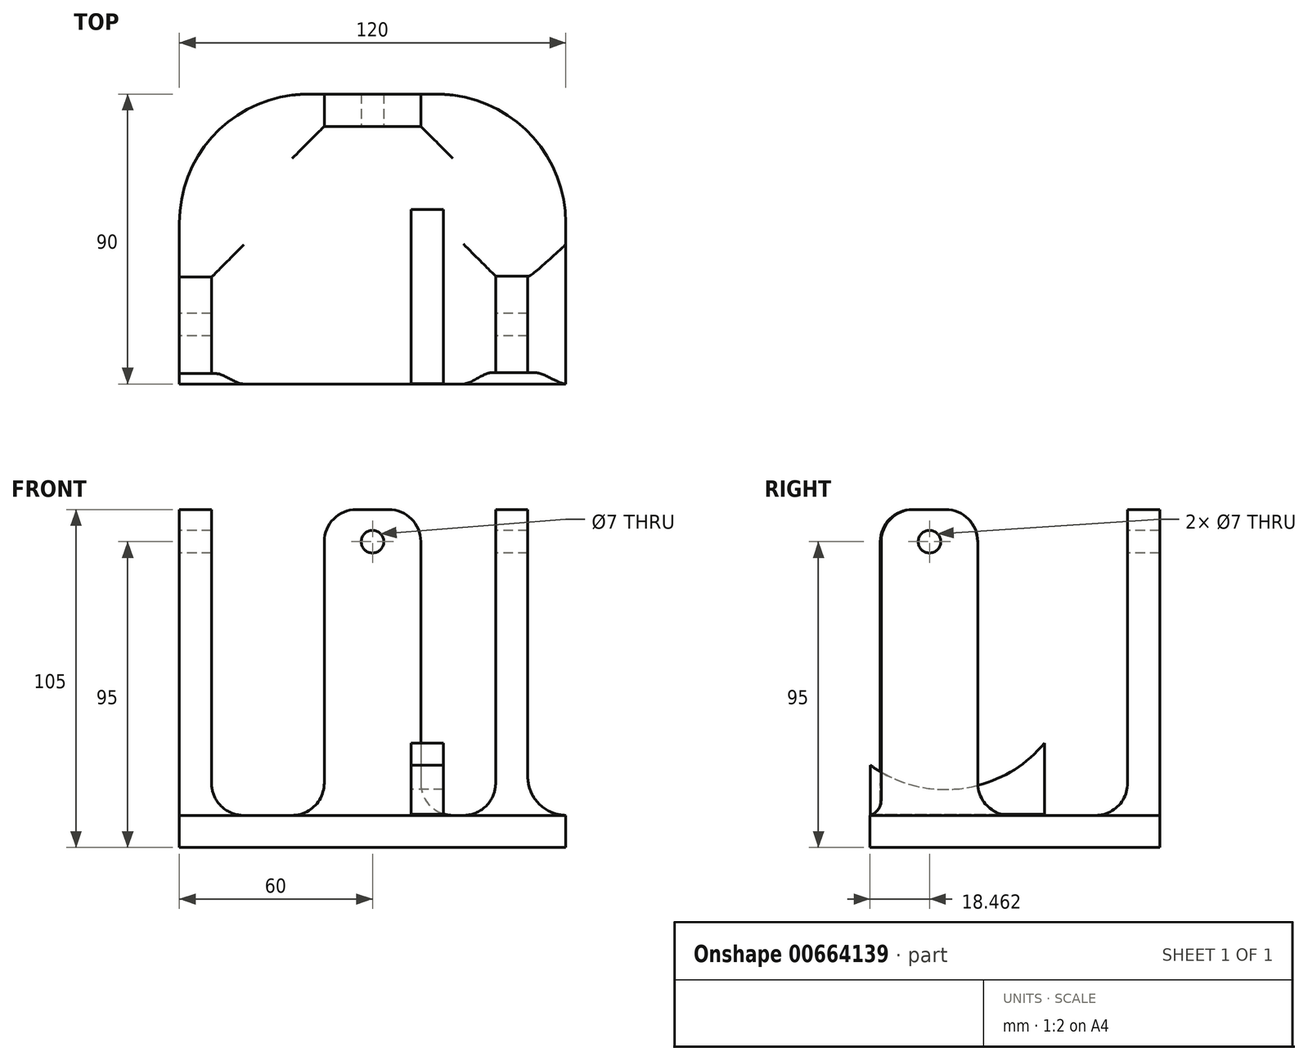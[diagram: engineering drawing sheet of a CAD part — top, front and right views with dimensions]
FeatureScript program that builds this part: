
annotation { "Feature Type Name" : "Feature", "Feature Type Description" : "" }
export const myFeature = defineFeature(function(context is Context, id is Id, definition is map)
    precondition{}
    {
        {
            var Q0;
            Q0=qCreatedBy(makeId("Top.planeOp"),FACE);
            var sketch = newSketch(context, id + "F0", { "sketchPlane" : qUnion([Q0])});
            skLineSegment(sketch, "E0.bottom", {"start": v(-20, 45) * mm, "end": v(20, 45) * mm});
            skLineSegment(sketch, "E0.top", {"start": v(-60, -45) * mm, "end": v(60, -45) * mm});
            skLineSegment(sketch, "E0.left", {"start": v(-60, 5) * mm, "end": v(-60, -45) * mm});
            skLineSegment(sketch, "E0.right", {"start": v(60, 5) * mm, "end": v(60, -45) * mm});
            skPoint(sketch, "E0.middle", {"position": v(0, 0) * mm});
            skPoint(sketch, "E1.visualSharp", {"position": v(-60, 45) * mm});
            skArc(sketch, "E1.filletArc", {"start": v(-20, 45) * mm, "mid": v(-48.28, 33.28) * mm, "end": v(-60, 5) * mm});
            skPoint(sketch, "E2.visualSharp", {"position": v(60, 45) * mm});
            skArc(sketch, "E2.filletArc", {"start": v(60, 5) * mm, "mid": v(48.28, 33.28) * mm, "end": v(20, 45) * mm});
            skSolve(sketch);
        }
        {
            var Q0;
            Q0=makeQuery(id+"F0.imprint","IMPRINT",FACE,{"disambiguationData":[TD([[makeQuery(id+"F0.imprint","IMPRINT",EDGE,{"derivedFrom":sQuery(id+"F0.wireOp",EDGE,"E0.bottom")}),-1.0]])]});
            extrude(context, id + "F1", {"entities" : qUnion([Q0]), "depth" : 10 * mm, "offsetDistance" : 25 * mm});
        }
        {
            var Q0;
            Q0=makeQuery(id+"F1.opExtrude","CAP_FACE",FACE,{"disambiguationData":[OSD([sQuery(id+"F0.wireOp",EDGE,"E0.bottom"),sQuery(id+"F0.wireOp",EDGE,"E0.top"),sQuery(id+"F0.wireOp",EDGE,"E0.left"),sQuery(id+"F0.wireOp",EDGE,"E0.right"),sQuery(id+"F0.wireOp",EDGE,"E1.filletArc"),sQuery(id+"F0.wireOp",EDGE,"E2.filletArc")])],"isStart":false});
            var sketch = newSketch(context, id + "F2", { "sketchPlane" : qUnion([Q0])});
            skSolve(sketch);
        }
        {
            var Q0;
            Q0=qCreatedBy(makeId("Top.planeOp"),FACE);
            var sketch = newSketch(context, id + "F3", { "sketchPlane" : qUnion([Q0])});
            skLineSegment(sketch, "E3.bottom", {"start": v(-60, -41.81) * mm, "end": v(-50, -41.81) * mm});
            skLineSegment(sketch, "E3.top", {"start": v(-60, -11.81) * mm, "end": v(-50, -11.81) * mm});
            skLineSegment(sketch, "E3.left", {"start": v(-60, -41.81) * mm, "end": v(-60, -11.81) * mm});
            skLineSegment(sketch, "E3.right", {"start": v(-50, -41.81) * mm, "end": v(-50, -11.81) * mm});
            skLineSegment(sketch, "E4.bottom", {"start": v(38.23, -41.54) * mm, "end": v(48.23, -41.54) * mm});
            skLineSegment(sketch, "E4.top", {"start": v(38.23, -11.54) * mm, "end": v(48.23, -11.54) * mm});
            skLineSegment(sketch, "E4.left", {"start": v(38.23, -41.54) * mm, "end": v(38.23, -11.54) * mm});
            skLineSegment(sketch, "E4.right", {"start": v(48.23, -41.54) * mm, "end": v(48.23, -11.54) * mm});
            skLineSegment(sketch, "E5.bottom", {"start": v(-15, 45) * mm, "end": v(15, 45) * mm});
            skLineSegment(sketch, "E5.top", {"start": v(-15, 35) * mm, "end": v(15, 35) * mm});
            skLineSegment(sketch, "E5.left", {"start": v(-15, 45) * mm, "end": v(-15, 35) * mm});
            skLineSegment(sketch, "E5.right", {"start": v(15, 45) * mm, "end": v(15, 35) * mm});
            skSolve(sketch);
        }
        {
            var Q0;
            Q0=qSketchRegion(id+"F3",true);
            extrude(context, id + "F4", {"entities" : qUnion([Q0]), "operationType" : NewBodyOperationType.ADD, "depth" : 25 * mm, "offsetDistance" : 25 * mm});
        }
        {
            var Q0;
            Q0=qSketchRegion(id+"F3",true);
            var Q1;
            Q1=makeQuery(id+"F4.opExtrude","CAP_FACE",FACE,{"disambiguationData":[OSD([sQuery(id+"F3.wireOp",EDGE,"E3.bottom"),sQuery(id+"F3.wireOp",EDGE,"E3.top"),sQuery(id+"F3.wireOp",EDGE,"E3.left"),sQuery(id+"F3.wireOp",EDGE,"E3.right")])],"isStart":false});
            var Q2;
            Q2=makeQuery(id+"F4.opExtrude","CAP_FACE",FACE,{"disambiguationData":[OSD([sQuery(id+"F3.wireOp",EDGE,"E5.bottom"),sQuery(id+"F3.wireOp",EDGE,"E5.top"),sQuery(id+"F3.wireOp",EDGE,"E5.left"),sQuery(id+"F3.wireOp",EDGE,"E5.right")])],"isStart":false});
            var Q3;
            Q3=makeQuery(id+"F4.opExtrude","CAP_FACE",FACE,{"disambiguationData":[OSD([sQuery(id+"F3.wireOp",EDGE,"E4.bottom"),sQuery(id+"F3.wireOp",EDGE,"E4.top"),sQuery(id+"F3.wireOp",EDGE,"E4.left"),sQuery(id+"F3.wireOp",EDGE,"E4.right")])],"isStart":false});
            extrude(context, id + "F5", {"entities" : qUnion([Q0, Q1, Q2, Q3]), "operationType" : NewBodyOperationType.ADD, "depth" : 80 * mm, "offsetDistance" : 25 * mm});
        }
        {
            var Q0;
            {var subQ0=sQuery(id+"F3.wireOp",EDGE,"E4.bottom");Q0=makeQuery(id+"F5.opExtrude","CAP_EDGE",EDGE,{"disambiguationData":[OSD([subQ0]),TDD([makeQuery(id+"F4.opExtrude","CAP_EDGE",EDGE,{"disambiguationData":[OSD([subQ0])],"isStart":false})])],"isStart":false});}
            var Q1;
            {var subQ0=sQuery(id+"F3.wireOp",EDGE,"E4.top");Q1=makeQuery(id+"F5.opExtrude","CAP_EDGE",EDGE,{"disambiguationData":[OSD([subQ0]),TDD([makeQuery(id+"F4.opExtrude","CAP_EDGE",EDGE,{"disambiguationData":[OSD([subQ0])],"isStart":false})])],"isStart":false});}
            fillet(context, id + "F6", {"entities" : qUnion([Q0, Q1]), "radius" : 10 * mm, "tangentPropagation" : true, "allowEdgeOverflow" : false});
        }
        {
            var Q0;
            {var subQ0=sQuery(id+"F3.wireOp",EDGE,"E5.right");Q0=makeQuery(id+"F5.opExtrude","CAP_EDGE",EDGE,{"disambiguationData":[OSD([subQ0]),TDD([makeQuery(id+"F4.opExtrude","CAP_EDGE",EDGE,{"disambiguationData":[OSD([subQ0])],"isStart":false})])],"isStart":false});}
            fillet(context, id + "F7", {"entities" : qUnion([Q0]), "radius" : 10 * mm, "tangentPropagation" : true, "allowEdgeOverflow" : false});
        }
        {
            var Q0;
            {var subQ0=sQuery(id+"F3.wireOp",EDGE,"E5.left");Q0=makeQuery(id+"F5.opExtrude","CAP_EDGE",EDGE,{"disambiguationData":[OSD([subQ0]),TDD([makeQuery(id+"F4.opExtrude","CAP_EDGE",EDGE,{"disambiguationData":[OSD([subQ0])],"isStart":false})])],"isStart":false});}
            fillet(context, id + "F8", {"entities" : qUnion([Q0]), "radius" : 10 * mm, "tangentPropagation" : true, "allowEdgeOverflow" : false});
        }
        {
            var Q0;
            {var subQ0=sQuery(id+"F3.wireOp",EDGE,"E3.top");Q0=makeQuery(id+"F5.opExtrude","CAP_EDGE",EDGE,{"disambiguationData":[OSD([subQ0]),TDD([makeQuery(id+"F4.opExtrude","CAP_EDGE",EDGE,{"disambiguationData":[OSD([subQ0])],"isStart":false})])],"isStart":false});}
            var Q1;
            {var subQ0=sQuery(id+"F3.wireOp",EDGE,"E3.bottom");Q1=makeQuery(id+"F5.opExtrude","CAP_EDGE",EDGE,{"disambiguationData":[OSD([subQ0]),TDD([makeQuery(id+"F4.opExtrude","CAP_EDGE",EDGE,{"disambiguationData":[OSD([subQ0])],"isStart":false})])],"isStart":false});}
            fillet(context, id + "F9", {"entities" : qUnion([Q0, Q1]), "radius" : 10 * mm, "tangentPropagation" : true, "allowEdgeOverflow" : false});
        }
        {
            var Q0;
            {var subQ0=sQuery(id+"F3.wireOp",EDGE,"E5.top");Q0=makeQuery(id+"F5.boolean.opBoolean","MERGE",FACE,{"derivedFrom":[makeQuery(id+"F4.opExtrude","SWEPT_FACE",FACE,{"disambiguationData":[OSD([subQ0])]}),makeQuery(id+"F5.opExtrude","SWEPT_FACE",FACE,{"disambiguationData":[OSD([subQ0]),TDD([makeQuery(id+"F3.imprint","IMPRINT",EDGE,{"derivedFrom":subQ0})])]}),makeQuery(id+"F5.opExtrude","SWEPT_FACE",FACE,{"disambiguationData":[OSD([subQ0]),TDD([makeQuery(id+"F4.opExtrude","CAP_EDGE",EDGE,{"disambiguationData":[OSD([subQ0])],"isStart":false})])]})]});}
            var sketch = newSketch(context, id + "F10", { "sketchPlane" : qUnion([Q0])});
            skCircle(sketch, "E6", {"center": v(0, 95) * mm, "radius": 3.5 * mm});
            skSolve(sketch);
        }
        {
            var Q0;
            Q0=sQuery(id+"F10.wireOp",VERTEX,"E6.center");
            var Q1;
            Q1=makeQuery(id+"F1.opExtrude","SWEPT_BODY",BODY,{"disambiguationData":[OSD([sQuery(id+"F0.wireOp",EDGE,"E0.bottom"),sQuery(id+"F0.wireOp",EDGE,"E0.top"),sQuery(id+"F0.wireOp",EDGE,"E0.left"),sQuery(id+"F0.wireOp",EDGE,"E0.right"),sQuery(id+"F0.wireOp",EDGE,"E1.filletArc"),sQuery(id+"F0.wireOp",EDGE,"E2.filletArc")])]});
            hole(context, id + "F11", {"style" : HoleStyle.SIMPLE, "endStyle" : HoleEndStyle.THROUGH, "holeDiameter" : 7 * mm, "majorDiameter" : 5 * mm, "isTappedThrough" : true, "tappedDepth" : 12 * mm, "tapClearance" : 3, "locations" : qUnion([Q0]), "scope" : qUnion([Q1])});
        }
        {
            var Q0;
            {var subQ0=sQuery(id+"F3.wireOp",EDGE,"E3.left");Q0=makeQuery(id+"F5.boolean.opBoolean","MERGE",FACE,{"derivedFrom":[makeQuery(id+"F4.boolean.opBoolean","MERGE",FACE,{"derivedFrom":[makeQuery(id+"F1.opExtrude","SWEPT_FACE",FACE,{"disambiguationData":[OSD([sQuery(id+"F0.wireOp",EDGE,"E0.left")])]}),makeQuery(id+"F4.opExtrude","SWEPT_FACE",FACE,{"disambiguationData":[OSD([subQ0])]})]}),makeQuery(id+"F5.opExtrude","SWEPT_FACE",FACE,{"disambiguationData":[OSD([subQ0]),TDD([makeQuery(id+"F3.imprint","IMPRINT",EDGE,{"derivedFrom":subQ0})])]}),makeQuery(id+"F5.opExtrude","SWEPT_FACE",FACE,{"disambiguationData":[OSD([subQ0]),TDD([makeQuery(id+"F4.opExtrude","CAP_EDGE",EDGE,{"disambiguationData":[OSD([subQ0])],"isStart":false})])]})]});}
            var sketch = newSketch(context, id + "F12", { "sketchPlane" : qUnion([Q0])});
            skCircle(sketch, "E7", {"center": v(26.54, 95) * mm, "radius": 3.5 * mm});
            skSolve(sketch);
        }
        {
            var Q0;
            Q0=sQuery(id+"F12.wireOp",VERTEX,"E7.center");
            var Q1;
            Q1=makeQuery(id+"F1.opExtrude","SWEPT_BODY",BODY,{"disambiguationData":[OSD([sQuery(id+"F0.wireOp",EDGE,"E0.bottom"),sQuery(id+"F0.wireOp",EDGE,"E0.top"),sQuery(id+"F0.wireOp",EDGE,"E0.left"),sQuery(id+"F0.wireOp",EDGE,"E0.right"),sQuery(id+"F0.wireOp",EDGE,"E1.filletArc"),sQuery(id+"F0.wireOp",EDGE,"E2.filletArc")])]});
            hole(context, id + "F13", {"style" : HoleStyle.SIMPLE, "endStyle" : HoleEndStyle.THROUGH, "holeDiameter" : 7 * mm, "majorDiameter" : 5 * mm, "isTappedThrough" : true, "tappedDepth" : 12 * mm, "tapClearance" : 3, "locations" : qUnion([Q0]), "scope" : qUnion([Q1])});
        }
        {
            var Q0;
            Q0=makeQuery(id+"F4.boolean.opBoolean","INTERSECT",EDGE,{"derivedFrom":[makeQuery(id+"F1.opExtrude","CAP_FACE",FACE,{"disambiguationData":[OSD([sQuery(id+"F0.wireOp",EDGE,"E0.bottom"),sQuery(id+"F0.wireOp",EDGE,"E0.top"),sQuery(id+"F0.wireOp",EDGE,"E0.left"),sQuery(id+"F0.wireOp",EDGE,"E0.right"),sQuery(id+"F0.wireOp",EDGE,"E1.filletArc"),sQuery(id+"F0.wireOp",EDGE,"E2.filletArc")])],"isStart":false}),makeQuery(id+"F4.opExtrude","SWEPT_FACE",FACE,{"disambiguationData":[OSD([sQuery(id+"F3.wireOp",EDGE,"E3.top")])]})]});
            fillet(context, id + "F14", {"entities" : qUnion([Q0]), "radius" : 10 * mm, "tangentPropagation" : true, "allowEdgeOverflow" : false});
        }
        {
            var Q0;
            Q0=makeQuery(id+"F4.boolean.opBoolean","INTERSECT",EDGE,{"derivedFrom":[makeQuery(id+"F1.opExtrude","CAP_FACE",FACE,{"disambiguationData":[OSD([sQuery(id+"F0.wireOp",EDGE,"E0.bottom"),sQuery(id+"F0.wireOp",EDGE,"E0.top"),sQuery(id+"F0.wireOp",EDGE,"E0.left"),sQuery(id+"F0.wireOp",EDGE,"E0.right"),sQuery(id+"F0.wireOp",EDGE,"E1.filletArc"),sQuery(id+"F0.wireOp",EDGE,"E2.filletArc")])],"isStart":false}),makeQuery(id+"F4.opExtrude","SWEPT_FACE",FACE,{"disambiguationData":[OSD([sQuery(id+"F3.wireOp",EDGE,"E5.left")])]})]});
            fillet(context, id + "F15", {"entities" : qUnion([Q0]), "radius" : 10 * mm, "tangentPropagation" : true, "allowEdgeOverflow" : false});
        }
        {
            var Q0;
            Q0=makeQuery(id+"F4.boolean.opBoolean","INTERSECT",EDGE,{"derivedFrom":[makeQuery(id+"F1.opExtrude","CAP_FACE",FACE,{"disambiguationData":[OSD([sQuery(id+"F0.wireOp",EDGE,"E0.bottom"),sQuery(id+"F0.wireOp",EDGE,"E0.top"),sQuery(id+"F0.wireOp",EDGE,"E0.left"),sQuery(id+"F0.wireOp",EDGE,"E0.right"),sQuery(id+"F0.wireOp",EDGE,"E1.filletArc"),sQuery(id+"F0.wireOp",EDGE,"E2.filletArc")])],"isStart":false}),makeQuery(id+"F4.opExtrude","SWEPT_FACE",FACE,{"disambiguationData":[OSD([sQuery(id+"F3.wireOp",EDGE,"E5.right")])]})]});
            var Q1;
            Q1=makeQuery(id+"F4.boolean.opBoolean","INTERSECT",EDGE,{"derivedFrom":[makeQuery(id+"F1.opExtrude","CAP_FACE",FACE,{"disambiguationData":[OSD([sQuery(id+"F0.wireOp",EDGE,"E0.bottom"),sQuery(id+"F0.wireOp",EDGE,"E0.top"),sQuery(id+"F0.wireOp",EDGE,"E0.left"),sQuery(id+"F0.wireOp",EDGE,"E0.right"),sQuery(id+"F0.wireOp",EDGE,"E1.filletArc"),sQuery(id+"F0.wireOp",EDGE,"E2.filletArc")])],"isStart":false}),makeQuery(id+"F4.opExtrude","SWEPT_FACE",FACE,{"disambiguationData":[OSD([sQuery(id+"F3.wireOp",EDGE,"E4.top")])]})]});
            fillet(context, id + "F16", {"entities" : qUnion([Q0, Q1]), "radius" : 10 * mm, "tangentPropagation" : true, "allowEdgeOverflow" : false});
        }
        {
            var Q0;
            Q0=makeQuery(id+"F4.boolean.opBoolean","INTERSECT",EDGE,{"derivedFrom":[makeQuery(id+"F1.opExtrude","CAP_FACE",FACE,{"disambiguationData":[OSD([sQuery(id+"F0.wireOp",EDGE,"E0.bottom"),sQuery(id+"F0.wireOp",EDGE,"E0.top"),sQuery(id+"F0.wireOp",EDGE,"E0.left"),sQuery(id+"F0.wireOp",EDGE,"E0.right"),sQuery(id+"F0.wireOp",EDGE,"E1.filletArc"),sQuery(id+"F0.wireOp",EDGE,"E2.filletArc")])],"isStart":false}),makeQuery(id+"F4.opExtrude","SWEPT_FACE",FACE,{"disambiguationData":[OSD([sQuery(id+"F3.wireOp",EDGE,"E4.right")])]})]});
            fillet(context, id + "F17", {"entities" : qUnion([Q0]), "radius" : 12 * mm, "tangentPropagation" : true, "allowEdgeOverflow" : false});
        }
        {
            var Q0;
            Q0=makeQuery(id+"F4.boolean.opBoolean","INTERSECT",EDGE,{"derivedFrom":[makeQuery(id+"F1.opExtrude","CAP_FACE",FACE,{"disambiguationData":[OSD([sQuery(id+"F0.wireOp",EDGE,"E0.bottom"),sQuery(id+"F0.wireOp",EDGE,"E0.top"),sQuery(id+"F0.wireOp",EDGE,"E0.left"),sQuery(id+"F0.wireOp",EDGE,"E0.right"),sQuery(id+"F0.wireOp",EDGE,"E1.filletArc"),sQuery(id+"F0.wireOp",EDGE,"E2.filletArc")])],"isStart":false}),makeQuery(id+"F4.opExtrude","SWEPT_FACE",FACE,{"disambiguationData":[OSD([sQuery(id+"F3.wireOp",EDGE,"E4.bottom")])]})]});
            fillet(context, id + "F18", {"entities" : qUnion([Q0]), "radius" : 5 * mm, "tangentPropagation" : true, "allowEdgeOverflow" : false});
        }
        {
            var Q0;
            Q0=makeQuery(id+"F4.boolean.opBoolean","INTERSECT",EDGE,{"derivedFrom":[makeQuery(id+"F1.opExtrude","CAP_FACE",FACE,{"disambiguationData":[OSD([sQuery(id+"F0.wireOp",EDGE,"E0.bottom"),sQuery(id+"F0.wireOp",EDGE,"E0.top"),sQuery(id+"F0.wireOp",EDGE,"E0.left"),sQuery(id+"F0.wireOp",EDGE,"E0.right"),sQuery(id+"F0.wireOp",EDGE,"E1.filletArc"),sQuery(id+"F0.wireOp",EDGE,"E2.filletArc")])],"isStart":false}),makeQuery(id+"F4.opExtrude","SWEPT_FACE",FACE,{"disambiguationData":[OSD([sQuery(id+"F3.wireOp",EDGE,"E3.right")])]})]});
            fillet(context, id + "F19", {"entities" : qUnion([Q0]), "radius" : 10 * mm, "tangentPropagation" : true, "allowEdgeOverflow" : false});
        }
        {
            var Q0;
            Q0=makeQuery(id+"F4.boolean.opBoolean","INTERSECT",EDGE,{"derivedFrom":[makeQuery(id+"F1.opExtrude","CAP_FACE",FACE,{"disambiguationData":[OSD([sQuery(id+"F0.wireOp",EDGE,"E0.bottom"),sQuery(id+"F0.wireOp",EDGE,"E0.top"),sQuery(id+"F0.wireOp",EDGE,"E0.left"),sQuery(id+"F0.wireOp",EDGE,"E0.right"),sQuery(id+"F0.wireOp",EDGE,"E1.filletArc"),sQuery(id+"F0.wireOp",EDGE,"E2.filletArc")])],"isStart":false}),makeQuery(id+"F4.opExtrude","SWEPT_FACE",FACE,{"disambiguationData":[OSD([sQuery(id+"F3.wireOp",EDGE,"E3.bottom")])]})]});
            fillet(context, id + "F20", {"entities" : qUnion([Q0]), "radius" : 5 * mm, "tangentPropagation" : true, "allowEdgeOverflow" : false});
        }
        {
            var Q0;
            Q0=makeQuery(id+"F4.boolean.opBoolean","INTERSECT",EDGE,{"derivedFrom":[makeQuery(id+"F1.opExtrude","CAP_FACE",FACE,{"disambiguationData":[OSD([sQuery(id+"F0.wireOp",EDGE,"E0.bottom"),sQuery(id+"F0.wireOp",EDGE,"E0.top"),sQuery(id+"F0.wireOp",EDGE,"E0.left"),sQuery(id+"F0.wireOp",EDGE,"E0.right"),sQuery(id+"F0.wireOp",EDGE,"E1.filletArc"),sQuery(id+"F0.wireOp",EDGE,"E2.filletArc")])],"isStart":false}),makeQuery(id+"F4.opExtrude","SWEPT_FACE",FACE,{"disambiguationData":[OSD([sQuery(id+"F3.wireOp",EDGE,"E5.top")])]})]});
            fillet(context, id + "F21", {"entities" : qUnion([Q0]), "radius" : 10 * mm, "tangentPropagation" : true, "allowEdgeOverflow" : false});
        }
        {
            var Q0;
            Q0=makeQuery(id+"F4.boolean.opBoolean","INTERSECT",EDGE,{"derivedFrom":[makeQuery(id+"F1.opExtrude","CAP_FACE",FACE,{"disambiguationData":[OSD([sQuery(id+"F0.wireOp",EDGE,"E0.bottom"),sQuery(id+"F0.wireOp",EDGE,"E0.top"),sQuery(id+"F0.wireOp",EDGE,"E0.left"),sQuery(id+"F0.wireOp",EDGE,"E0.right"),sQuery(id+"F0.wireOp",EDGE,"E1.filletArc"),sQuery(id+"F0.wireOp",EDGE,"E2.filletArc")])],"isStart":false}),makeQuery(id+"F4.opExtrude","SWEPT_FACE",FACE,{"disambiguationData":[OSD([sQuery(id+"F3.wireOp",EDGE,"E4.left")])]})]});
            fillet(context, id + "F22", {"entities" : qUnion([Q0]), "radius" : 10 * mm, "tangentPropagation" : true, "allowEdgeOverflow" : false});
        }
        {
            var Q0;
            Q0=makeQuery(id+"F2.imprint","IMPRINT",FACE,{"disambiguationData":[TD([[makeQuery(id+"F2.imprint","IMPRINT",EDGE,{"derivedFrom":makeQuery(id+"F1.opExtrude","CAP_EDGE",EDGE,{"disambiguationData":[OSD([sQuery(id+"F0.wireOp",EDGE,"E0.bottom")])],"isStart":false})}),-1.0]])]});
            var sketch = newSketch(context, id + "F23", { "sketchPlane" : qUnion([Q0])});
            skLineSegment(sketch, "E8.bottom", {"start": v(11.98, -45) * mm, "end": v(21.98, -45) * mm});
            skLineSegment(sketch, "E8.top", {"start": v(11.98, 10) * mm, "end": v(21.98, 10) * mm});
            skLineSegment(sketch, "E8.left", {"start": v(11.98, -45) * mm, "end": v(11.98, 10) * mm});
            skLineSegment(sketch, "E8.right", {"start": v(21.98, -45) * mm, "end": v(21.98, 10) * mm});
            skSolve(sketch);
        }
        {
            var Q0;
            Q0=qCreatedBy(makeId("Right.planeOp"),FACE);
            cPlane(context, id + "F24", {"entities" : qUnion([Q0]), "cplaneType" : CPlaneType.OFFSET, "offset" : 12 * mm, "width" : 150 * mm, "height" : 150 * mm});
        }
        {
            var Q0;
            Q0=qCreatedBy(id+"F24.planeOp",FACE);
            var sketch = newSketch(context, id + "F25", { "sketchPlane" : qUnion([Q0])});
            skLineSegment(sketch, "E9", {"start": v(-44.9, 10.36) * mm, "end": v(-44.9, 25.6) * mm});
            skLineSegment(sketch, "E10", {"start": v(-44.9, 10.36) * mm, "end": v(9.18, 10.36) * mm});
            skLineSegment(sketch, "E11", {"start": v(9.18, 10.36) * mm, "end": v(9.18, 32.44) * mm});
            skArc(sketch, "E12", {"start": v(-44.9, 25.6) * mm, "mid": v(-16.51, 18.34) * mm, "end": v(9.18, 32.44) * mm});
            skSolve(sketch);
        }
        {
            var Q0;
            Q0=makeQuery(id+"F25.imprint","IMPRINT",FACE,{"disambiguationData":[TD([[makeQuery(id+"F25.imprint","IMPRINT",EDGE,{"derivedFrom":sQuery(id+"F25.wireOp",EDGE,"E9")}),-1.0]])]});
            extrude(context, id + "F26", {"entities" : qUnion([Q0]), "depth" : 10 * mm, "offsetDistance" : 25 * mm});
        }
    });
